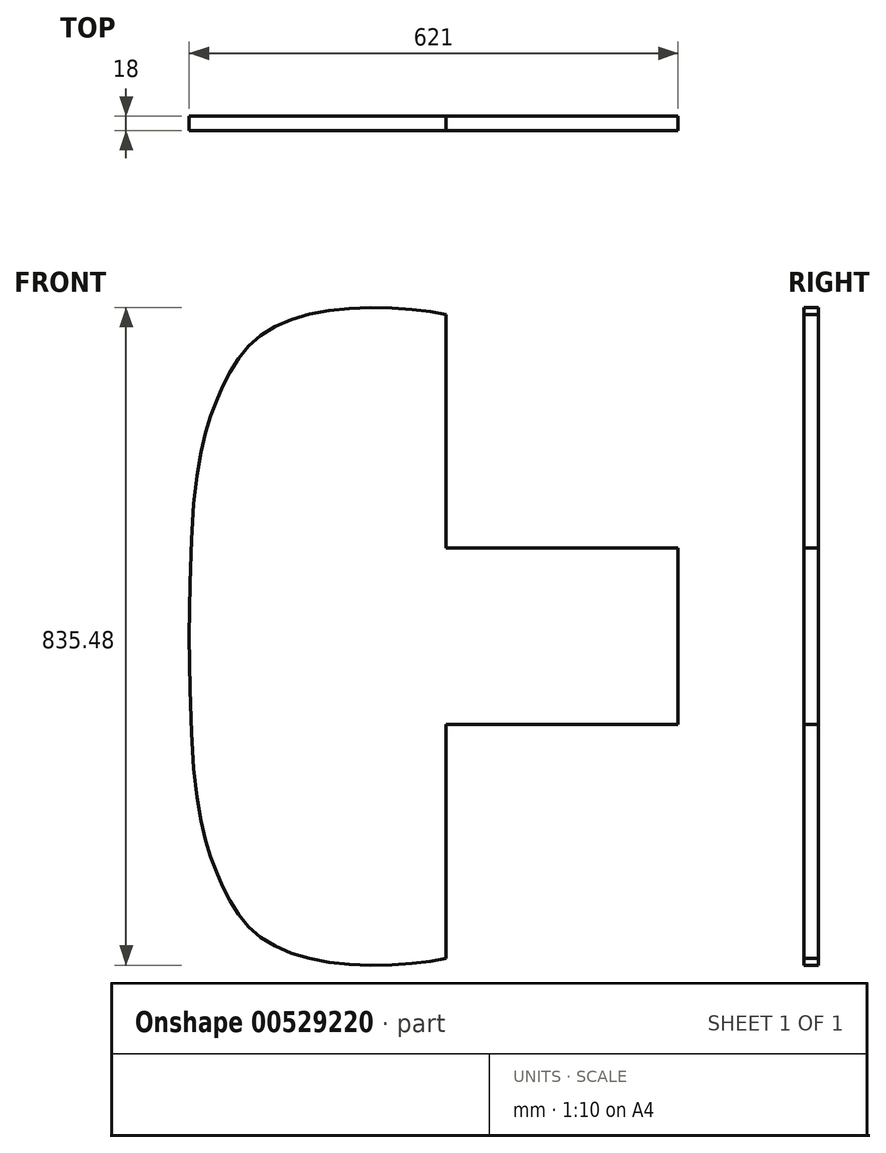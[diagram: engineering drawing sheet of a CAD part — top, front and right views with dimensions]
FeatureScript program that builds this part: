
annotation { "Feature Type Name" : "Feature", "Feature Type Description" : "" }
export const myFeature = defineFeature(function(context is Context, id is Id, definition is map)
    precondition{}
    {
        {
            var Q0;
            Q0=qCreatedBy(makeId("Front.planeOp"),FACE);
            var sketch = newSketch(context, id + "F0", { "sketchPlane" : qUnion([Q0])});
            skLineSegment(sketch, "E0", {"start": v(-355.6, 0) * mm, "end": v(355.6, 0) * mm, "construction": true});
            skLineSegment(sketch, "E1.0.1.0", {"start": v(-355.6, 50.8) * mm, "end": v(355.6, 50.8) * mm, "construction": true});
            skLineSegment(sketch, "E1.0.2.0", {"start": v(-355.6, 101.6) * mm, "end": v(355.6, 101.6) * mm, "construction": true});
            skLineSegment(sketch, "E1.0.3.0", {"start": v(-355.6, 152.4) * mm, "end": v(355.6, 152.4) * mm, "construction": true});
            skLineSegment(sketch, "E1.0.4.0", {"start": v(-355.6, 203.2) * mm, "end": v(355.6, 203.2) * mm, "construction": true});
            skLineSegment(sketch, "E1.0.5.0", {"start": v(-355.6, 254) * mm, "end": v(355.6, 254) * mm, "construction": true});
            skLineSegment(sketch, "E1.direction1", {"start": v(-355.6, 0) * mm, "end": v(-330.6, 0) * mm, "construction": true});
            skLineSegment(sketch, "E1.direction2", {"start": v(-355.6, 0) * mm, "end": v(-355.6, 50.8) * mm, "construction": true});
            skLineSegment(sketch, "E2.0.1.0", {"start": v(-355.6, -50.8) * mm, "end": v(355.6, -50.8) * mm, "construction": true});
            skLineSegment(sketch, "E2.0.2.0", {"start": v(-355.6, -101.6) * mm, "end": v(355.6, -101.6) * mm, "construction": true});
            skLineSegment(sketch, "E2.0.3.0", {"start": v(-355.6, -152.4) * mm, "end": v(355.6, -152.4) * mm, "construction": true});
            skLineSegment(sketch, "E2.0.4.0", {"start": v(-355.6, -203.2) * mm, "end": v(355.6, -203.2) * mm, "construction": true});
            skLineSegment(sketch, "E2.0.5.0", {"start": v(-355.6, -254) * mm, "end": v(355.6, -254) * mm, "construction": true});
            skLineSegment(sketch, "E2.direction1", {"start": v(-355.6, 0) * mm, "end": v(0, 0) * mm, "construction": true});
            skLineSegment(sketch, "E2.direction2", {"start": v(-355.6, 0) * mm, "end": v(-355.6, -50.8) * mm, "construction": true});
            skLineSegment(sketch, "E3", {"start": v(0, 254) * mm, "end": v(0, -254) * mm, "construction": true});
            skLineSegment(sketch, "E4.1.0.0", {"start": v(50.8, 254) * mm, "end": v(50.8, -254) * mm, "construction": true});
            skLineSegment(sketch, "E4.2.0.0", {"start": v(101.6, 254) * mm, "end": v(101.6, -254) * mm, "construction": true});
            skLineSegment(sketch, "E4.3.0.0", {"start": v(152.4, 254) * mm, "end": v(152.4, -254) * mm, "construction": true});
            skLineSegment(sketch, "E4.4.0.0", {"start": v(203.2, 254) * mm, "end": v(203.2, -254) * mm, "construction": true});
            skLineSegment(sketch, "E4.5.0.0", {"start": v(254, 254) * mm, "end": v(254, -254) * mm, "construction": true});
            skLineSegment(sketch, "E4.6.0.0", {"start": v(304.8, 254) * mm, "end": v(304.8, -254) * mm, "construction": true});
            skLineSegment(sketch, "E4.7.0.0", {"start": v(355.6, 254) * mm, "end": v(355.6, -254) * mm, "construction": true});
            skLineSegment(sketch, "E4.direction1", {"start": v(0, -254) * mm, "end": v(50.8, -254) * mm, "construction": true});
            skLineSegment(sketch, "E5.1.0.0", {"start": v(-50.8, 254) * mm, "end": v(-50.8, -254) * mm, "construction": true});
            skLineSegment(sketch, "E5.2.0.0", {"start": v(-101.6, 254) * mm, "end": v(-101.6, -254) * mm, "construction": true});
            skLineSegment(sketch, "E5.3.0.0", {"start": v(-152.4, 254) * mm, "end": v(-152.4, -254) * mm, "construction": true});
            skLineSegment(sketch, "E5.4.0.0", {"start": v(-203.2, 254) * mm, "end": v(-203.2, -254) * mm, "construction": true});
            skLineSegment(sketch, "E5.5.0.0", {"start": v(-254, 254) * mm, "end": v(-254, -254) * mm, "construction": true});
            skLineSegment(sketch, "E5.6.0.0", {"start": v(-304.8, 254) * mm, "end": v(-304.8, -254) * mm, "construction": true});
            skLineSegment(sketch, "E5.7.0.0", {"start": v(-355.6, 254) * mm, "end": v(-355.6, -254) * mm, "construction": true});
            skLineSegment(sketch, "E5.direction1", {"start": v(0, -254) * mm, "end": v(-50.8, -254) * mm, "construction": true});
            skLineSegment(sketch, "E6", {"start": v(-326, -217) * mm, "end": v(295, -217) * mm});
            skLineSegment(sketch, "E7", {"start": v(295, -217) * mm, "end": v(295, -105) * mm});
            skLineSegment(sketch, "E8", {"start": v(295, -105) * mm, "end": v(0, -105) * mm});
            skLineSegment(sketch, "E9", {"start": v(0, -105) * mm, "end": v(0, 192) * mm});
            skFitSpline(sketch, "E10", {"points": [v(0, 192) * mm, v(-133.07, 198.87) * mm, v(-242.33, 159.56) * mm, v(-290.3, 84.99) * mm, v(-326, -217) * mm], "startDerivative": vector(-407.73, 87.78) * mm, "endDerivative": vector(-4.48, -1695.42) * mm});
            skFitSpline(sketch, "E11.MirrorCS", {"points": [v(0, -626) * mm, v(-133.07, -632.87) * mm, v(-242.33, -593.56) * mm, v(-290.3, -518.99) * mm, v(-326, -217) * mm], "startDerivative": vector(-407.73, -87.78) * mm, "endDerivative": vector(-4.48, 1695.42) * mm});
            skLineSegment(sketch, "E12.MirrorCS", {"start": v(0, -329) * mm, "end": v(0, -626) * mm});
            skLineSegment(sketch, "E13.MirrorCS", {"start": v(295, -329) * mm, "end": v(0, -329) * mm});
            skLineSegment(sketch, "E14.MirrorCS", {"start": v(295, -217) * mm, "end": v(295, -329) * mm});
            skSolve(sketch);
        }
        {
            var Q0;
            Q0=makeQuery(id+"F0.imprint","IMPRINT",FACE,{"disambiguationData":[TD([[makeQuery(id+"F0.imprint","IMPRINT",EDGE,{"derivedFrom":sQuery(id+"F0.wireOp",EDGE,"E6")}),-1.0]])]});
            var Q1;
            Q1=makeQuery(id+"F0.imprint","IMPRINT",FACE,{"disambiguationData":[TD([[makeQuery(id+"F0.imprint","IMPRINT",EDGE,{"derivedFrom":sQuery(id+"F0.wireOp",EDGE,"E6")}),1.0]])]});
            extrude(context, id + "F1", {"entities" : qUnion([Q0, Q1]), "depth" : 18 * mm, "offsetDistance" : 25 * mm});
        }
        {
            var Q0;
            Q0=makeQuery(id+"F1.opExtrude","SWEPT_EDGE",EDGE,{"disambiguationData":[OSD([sQuery(id+"F0.wireOp",EDGE,"E6"),sQuery(id+"F0.wireOp",EDGE,"E10"),sQuery(id+"F0.wireOp",EDGE,"E11.MirrorCS")])]});
            fillet(context, id + "F2", {"entities" : qUnion([Q0]), "radius" : 100 * mm, "tangentPropagation" : true, "allowEdgeOverflow" : false});
        }
    });
